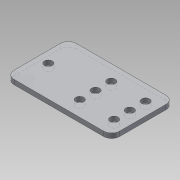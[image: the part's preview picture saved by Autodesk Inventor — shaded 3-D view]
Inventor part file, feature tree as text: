
AUTODESK INVENTOR PART (.ipt)
format: ipt  version: 2013 SP2 (Build 170200200, 200)  size: 111,616 bytes
history: native  units: mm
features: sketch x2, extrude x1, hole x1, fillet x1
ambient origin geometry x8: Origin, YZ Plane, XZ Plane, XY Plane, X Axis, Y Axis, Z Axis, Center Point
bodies: Solid1 (feature_tree)
feature tree (5):
  extrude  "Extrusion1"  Depth=39.5mm
  hole  "Hole1"  [1 undecoded]
  fillet  "Fillet1"  Radius=37.01mm
  sketch  "Sketch2"  dims[d0=67.0mm d1=39.5mm]
  sketch  "Sketch3"  dims[d2=3.0mm d3=0.0mm d4=7.06mm d5=37.01mm d6=58.79mm d7=9.75mm d8=9.75mm d9=21.78mm d10=19.75mm d11=5.1mm d12=6.0mm d13=4.0mm d14=2.0mm d15=90.0deg d16=8.0mm d17=20.594885mm d18=5.0mm]
note: 1 required parameter value undecoded (feature->parameter linkage not recoverable at this tier; creation-order binding heuristic only, values carry confidence <= 0.55)
